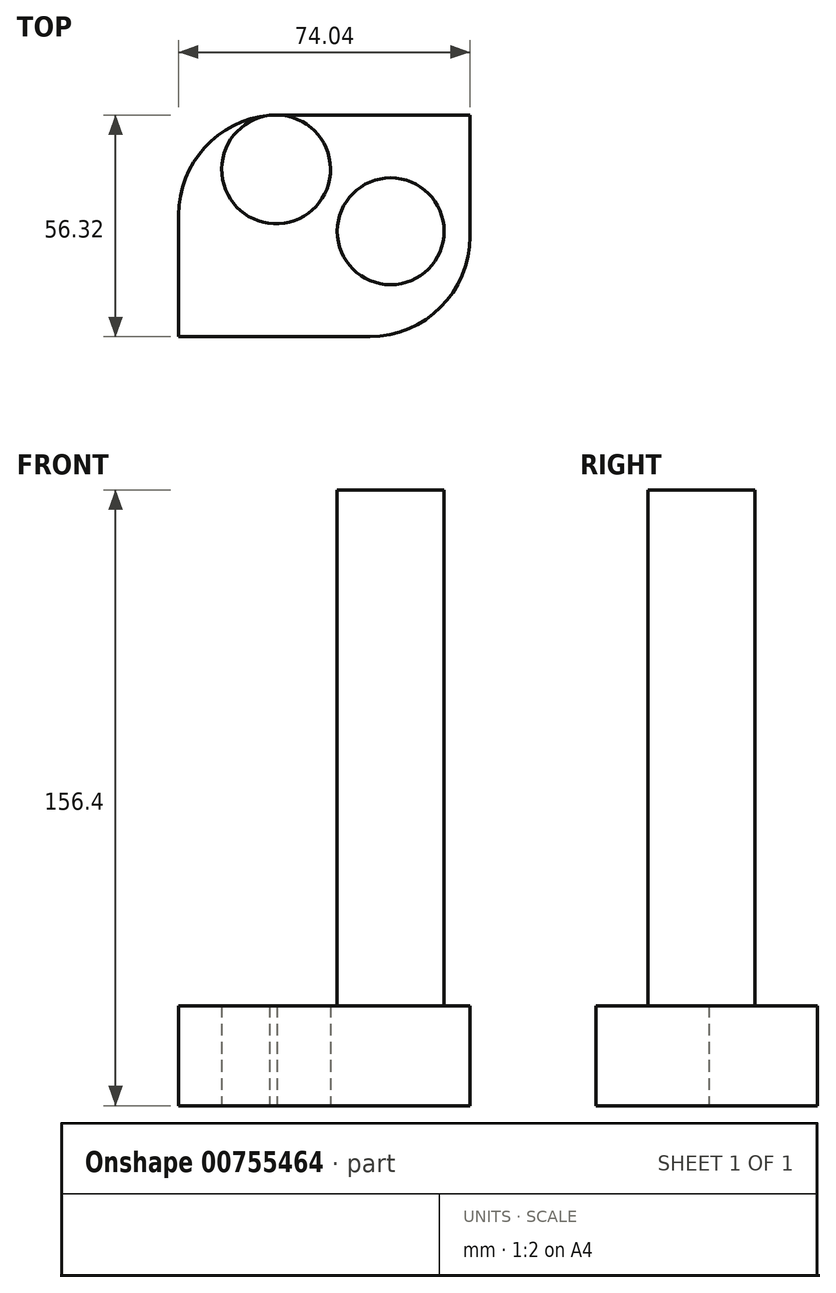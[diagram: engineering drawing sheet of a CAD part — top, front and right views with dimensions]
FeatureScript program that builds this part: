
annotation { "Feature Type Name" : "Feature", "Feature Type Description" : "" }
export const myFeature = defineFeature(function(context is Context, id is Id, definition is map)
    precondition{}
    {
        {
            var Q0;
            Q0=qCreatedBy(makeId("Top.planeOp"),FACE);
            var sketch = newSketch(context, id + "F0", { "sketchPlane" : qUnion([Q0])});
            skLineSegment(sketch, "E0.bottom", {"start": v(-24.78, 0) * mm, "end": v(23.86, 0) * mm});
            skLineSegment(sketch, "E0.top", {"start": v(0.62, 56.32) * mm, "end": v(49.26, 56.32) * mm});
            skLineSegment(sketch, "E0.left", {"start": v(-24.78, 0) * mm, "end": v(-24.78, 30.92) * mm});
            skLineSegment(sketch, "E0.right", {"start": v(49.26, 25.4) * mm, "end": v(49.26, 56.32) * mm});
            skCircle(sketch, "E1", {"center": v(0, 42.5) * mm, "radius": 13.82 * mm});
            skPoint(sketch, "E2.visualSharp", {"position": v(49.26, 0) * mm});
            skArc(sketch, "E2.filletArc", {"start": v(23.86, 0) * mm, "mid": v(41.82, 7.44) * mm, "end": v(49.26, 25.4) * mm});
            skPoint(sketch, "E3.visualSharp", {"position": v(-24.78, 56.32) * mm});
            skArc(sketch, "E3.filletArc", {"start": v(0.62, 56.32) * mm, "mid": v(-17.34, 48.88) * mm, "end": v(-24.78, 30.92) * mm});
            skSolve(sketch);
        }
        {
            var Q0;
            {var subQ0=sQuery(id+"F0.wireOp",EDGE,"E3.filletArc");var subQ1=sQuery(id+"F0.wireOp",EDGE,"E1");var subQ2=makeQuery(id+"F0.imprint","INTERSECT",VERTEX,{"disambiguationData":[OD(0.0)],"derivedFrom":[subQ1,subQ0]});Q0=makeQuery(id+"F0.imprint","IMPRINT",FACE,{"disambiguationData":[TD([[makeQuery(id+"F0.imprint","IMPRINT",EDGE,{"disambiguationData":[TD([[subQ2,-1.0]])],"derivedFrom":subQ1}),1.0]])]});}
            var Q1;
            Q1=makeQuery(id+"F0.imprint","IMPRINT",FACE,{"disambiguationData":[TD([[makeQuery(id+"F0.imprint","IMPRINT",EDGE,{"derivedFrom":sQuery(id+"F0.wireOp",EDGE,"E0.bottom")}),1.0]])]});
            extrude(context, id + "F1", {"entities" : qUnion([Q0, Q1]), "depth" : 25.4 * mm, "offsetDistance" : 25.4 * mm});
        }
        {
            var Q0;
            Q0=makeQuery(id+"F1.opExtrude","CAP_FACE",FACE,{"disambiguationData":[OSD([sQuery(id+"F0.wireOp",EDGE,"E0.bottom"),sQuery(id+"F0.wireOp",EDGE,"E0.top"),sQuery(id+"F0.wireOp",EDGE,"E0.left"),sQuery(id+"F0.wireOp",EDGE,"E0.right"),sQuery(id+"F0.wireOp",EDGE,"E1"),sQuery(id+"F0.wireOp",EDGE,"E2.filletArc"),sQuery(id+"F0.wireOp",EDGE,"E3.filletArc")])],"isStart":false});
            var sketch = newSketch(context, id + "F2", { "sketchPlane" : qUnion([Q0])});
            skCircle(sketch, "E4", {"center": v(29.1, 26.76) * mm, "radius": 13.57 * mm});
            skSolve(sketch);
        }
        {
            var Q0;
            Q0 = qSketchRegion(id + "F2", true);
            extrude(context, id + "F3", {"entities" : qUnion([Q0]), "operationType" : NewBodyOperationType.ADD, "depth" : 131 * mm, "offsetDistance" : 25 * mm});
        }
    });
